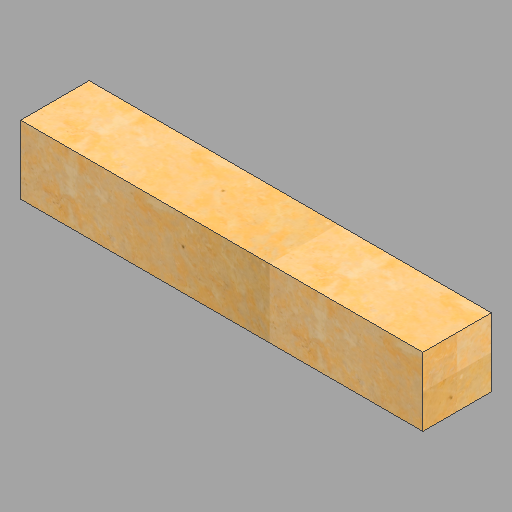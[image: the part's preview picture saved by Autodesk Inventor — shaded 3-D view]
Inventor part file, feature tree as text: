
AUTODESK INVENTOR PART (.ipt)
format: ipt  version: 2023 (Build 270158030, 158C)  size: 243,712 bytes
history: native  units: in
note: dims shown in document units (in); Inventor stores cm internally (conversion verified against a paired STEP export)
features: extrude x1, sketch x1
ambient origin geometry x8: Origin, YZ Plane, XZ Plane, XY Plane, X Axis, Y Axis, Z Axis, Center Point
bodies: Solid1 (feature_tree)
feature tree (2):
  extrude  "Extrusion1"  Depth=8.0in
  sketch  "Sketch1"  dims[d0=8.0in d1=8.0in d2=47.0in d3=0.0in]
